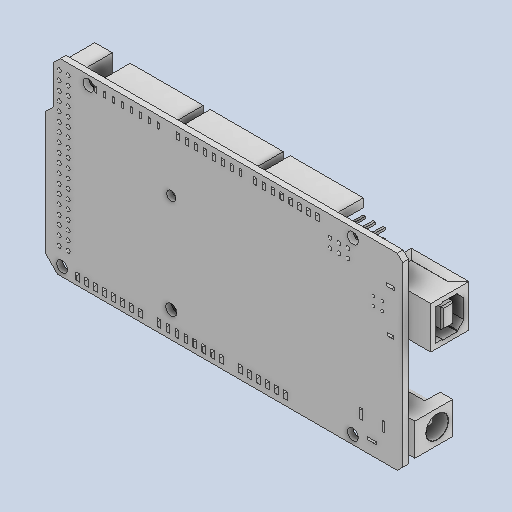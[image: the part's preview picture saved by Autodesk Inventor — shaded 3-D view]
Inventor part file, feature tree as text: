
AUTODESK INVENTOR PART (.ipt)
format: ipt  version: 2022 (Build 260153000, 153)  size: 1,272,832 bytes
history: native  units: in
note: dims shown in document units (in); Inventor stores cm internally (conversion verified against a paired STEP export)
features: fillet x1
ambient origin geometry x8: Origin, YZ Plane, XZ Plane, XY Plane, X Axis, Y Axis, Z Axis, Center Point
bodies: Solid1 (feature_tree)
feature tree (1):
  fillet  "Fillet5"  [1 undecoded]
note: 1 required parameter value undecoded (feature->parameter linkage not recoverable at this tier; creation-order binding heuristic only, values carry confidence <= 0.55)
